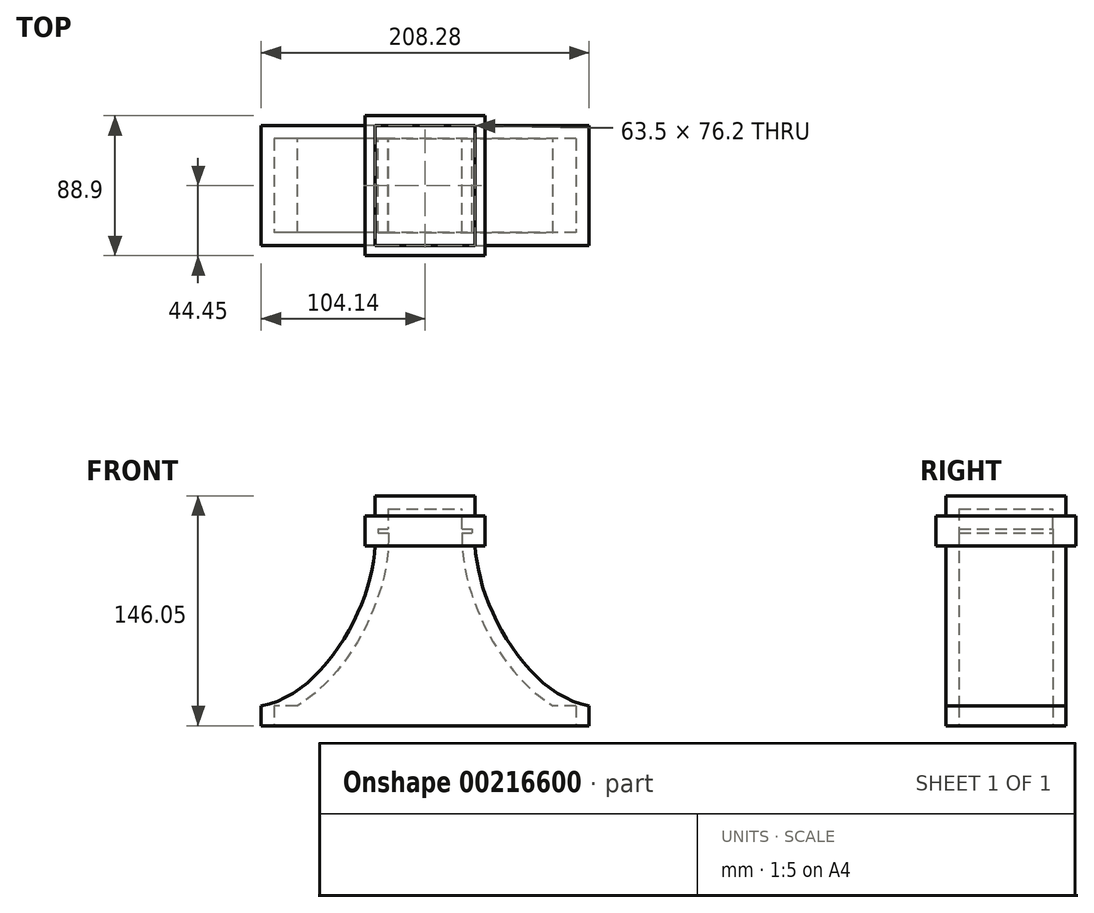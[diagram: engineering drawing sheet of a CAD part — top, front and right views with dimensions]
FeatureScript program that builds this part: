
annotation { "Feature Type Name" : "Feature", "Feature Type Description" : "" }
export const myFeature = defineFeature(function(context is Context, id is Id, definition is map)
    precondition{}
    {
        {
            var Q0;
            Q0=qCreatedBy(makeId("Top.planeOp"),FACE);
            var sketch = newSketch(context, id + "F0", { "sketchPlane" : qUnion([Q0])});
            skLineSegment(sketch, "E0.bottom", {"start": v(104.14, -38.1) * mm, "end": v(-104.14, -38.1) * mm});
            skLineSegment(sketch, "E0.top", {"start": v(104.14, 38.1) * mm, "end": v(-104.14, 38.1) * mm});
            skLineSegment(sketch, "E0.left", {"start": v(104.14, -38.1) * mm, "end": v(104.14, 38.1) * mm});
            skLineSegment(sketch, "E0.right", {"start": v(-104.14, -38.1) * mm, "end": v(-104.14, 38.1) * mm});
            skPoint(sketch, "E0.middle", {"position": v(0, 0) * mm});
            skLineSegment(sketch, "E1.bottom", {"start": v(95.88, 29.85) * mm, "end": v(-95.88, 29.85) * mm});
            skLineSegment(sketch, "E1.top", {"start": v(95.88, -29.85) * mm, "end": v(-95.88, -29.85) * mm});
            skLineSegment(sketch, "E1.left", {"start": v(95.88, 29.84) * mm, "end": v(95.88, -29.85) * mm});
            skLineSegment(sketch, "E1.right", {"start": v(-95.88, 29.85) * mm, "end": v(-95.88, -29.84) * mm});
            skSolve(sketch);
        }
        {
            var Q0;
            Q0=makeQuery(id+"F0.imprint","IMPRINT",FACE,{"disambiguationData":[TD([[makeQuery(id+"F0.imprint","IMPRINT",EDGE,{"derivedFrom":sQuery(id+"F0.wireOp",EDGE,"E0.bottom")}),-1.0]])]});
            extrude(context, id + "F1", {"entities" : qUnion([Q0]), "depth" : 12.7 * mm});
        }
        {
            var Q0;
            Q0=qCreatedBy(makeId("Front.planeOp"),FACE);
            var sketch = newSketch(context, id + "F2", { "sketchPlane" : qUnion([Q0])});
            skLineSegment(sketch, "E2", {"start": v(0, 0) * mm, "end": v(0, 146.05) * mm, "construction": true});
            skLineSegment(sketch, "E3", {"start": v(-31.75, 146.05) * mm, "end": v(31.75, 146.05) * mm});
            skLineSegment(sketch, "E4", {"start": v(-31.75, 146.05) * mm, "end": v(-31.75, 133.35) * mm});
            skLineSegment(sketch, "E5", {"start": v(-31.75, 133.35) * mm, "end": v(31.75, 133.35) * mm});
            skLineSegment(sketch, "E6", {"start": v(31.75, 133.35) * mm, "end": v(31.75, 146.05) * mm});
            skLineSegment(sketch, "E7.bottom", {"start": v(-38.1, 133.35) * mm, "end": v(38.1, 133.35) * mm});
            skLineSegment(sketch, "E7.top", {"start": v(-38.1, 114.3) * mm, "end": v(38.1, 114.3) * mm});
            skLineSegment(sketch, "E7.left", {"start": v(-38.1, 133.35) * mm, "end": v(-38.1, 114.3) * mm});
            skLineSegment(sketch, "E7.right", {"start": v(38.1, 133.35) * mm, "end": v(38.1, 114.3) * mm});
            skPoint(sketch, "E8", {"position": v(0, 114.3) * mm});
            skLineSegment(sketch, "E9", {"start": v(-31.75, 133.35) * mm, "end": v(-31.75, 114.3) * mm, "construction": true});
            skLineSegment(sketch, "E10", {"start": v(31.75, 133.35) * mm, "end": v(31.75, 114.3) * mm, "construction": true});
            skLineSegment(sketch, "E11", {"start": v(-104.14, 12.7) * mm, "end": v(104.14, 12.7) * mm});
            skFitSpline(sketch, "E12", {"points": [v(-31.75, 114.3) * mm, v(-104.14, 12.7) * mm], "startDerivative": vector(-3.4, -108.29) * mm, "endDerivative": vector(-120.63, -20.5) * mm});
            skFitSpline(sketch, "E13.MirrorCS", {"points": [v(31.75, 114.3) * mm, v(104.14, 12.7) * mm], "startDerivative": vector(3.4, -108.29) * mm, "endDerivative": vector(120.63, -20.5) * mm});
            skSolve(sketch);
        }
        {
            var Q0;
            Q0 = qSketchRegion(id + "F2", true);
            var Q1;
            Q1=makeQuery(id+"F1.opExtrude","SWEPT_FACE",FACE,{"disambiguationData":[OSD([sQuery(id+"F0.wireOp",EDGE,"E0.bottom")])]});
            var Q2;
            Q2=makeQuery(id+"F1.opExtrude","SWEPT_FACE",FACE,{"disambiguationData":[OSD([sQuery(id+"F0.wireOp",EDGE,"E0.top")])]});
            extrude(context, id + "F3", {"entities" : qUnion([Q0]), "endBound" : BoundingType.UP_TO_SURFACE, "endBoundEntityFace" : qUnion([Q1]), "depth" : 25.4 * mm, "hasSecondDirection" : true, "secondDirectionBound" : SecondDirectionBoundingType.UP_TO_SURFACE, "secondDirectionOppositeDirection" : true, "secondDirectionBoundEntityFace" : qUnion([Q2]), "secondDirectionDepth" : 25.4 * mm});
        }
        {
            var Q0;
            Q0=makeQuery(id+"F3.opExtrude","SWEPT_FACE",FACE,{"disambiguationData":[OSD([sQuery(id+"F2.wireOp",EDGE,"E11")])]});
            shell(context, id + "F4", {"entities" : qUnion([Q0]), "thickness" : 8.25 * mm});
        }
        {
            var Q0;
            Q0=makeQuery(id+"F1.opExtrude","SWEPT_BODY",BODY,{"disambiguationData":[OSD([sQuery(id+"F0.wireOp",EDGE,"E0.bottom"),sQuery(id+"F0.wireOp",EDGE,"E0.top"),sQuery(id+"F0.wireOp",EDGE,"E0.left"),sQuery(id+"F0.wireOp",EDGE,"E0.right"),sQuery(id+"F0.wireOp",EDGE,"E1.bottom"),sQuery(id+"F0.wireOp",EDGE,"E1.top"),sQuery(id+"F0.wireOp",EDGE,"E1.left"),sQuery(id+"F0.wireOp",EDGE,"E1.right")])]});
            var Q1;
            Q1=makeQuery(id+"F3.opExtrude","SWEPT_BODY",BODY,{"disambiguationData":[OSD([sQuery(id+"F2.wireOp",EDGE,"E3"),sQuery(id+"F2.wireOp",EDGE,"E4"),sQuery(id+"F2.wireOp",EDGE,"E6"),sQuery(id+"F2.wireOp",EDGE,"E7.bottom"),sQuery(id+"F2.wireOp",EDGE,"E7.top"),sQuery(id+"F2.wireOp",EDGE,"E7.left"),sQuery(id+"F2.wireOp",EDGE,"E7.right"),sQuery(id+"F2.wireOp",EDGE,"E11"),sQuery(id+"F2.wireOp",EDGE,"E12"),sQuery(id+"F2.wireOp",EDGE,"E13.MirrorCS")])]});
            booleanBodies(context, id + "F5", {"operationType" : BooleanOperationType.UNION, "tools" : qUnion([Q0, Q1])});
        }
        {
            var Q0;
            {var subQ0=sQuery(id+"F0.wireOp",EDGE,"E0.top");Q0=makeQuery(id+"F5.opBoolean","MERGE",FACE,{"derivedFrom":[makeQuery(id+"F1.opExtrude","SWEPT_FACE",FACE,{"disambiguationData":[OSD([subQ0])]}),makeQuery(id+"F3.opExtrude","CAP_FACE",FACE,{"disambiguationData":[OSD([subQ0])],"isStart":true})]});}
            var sketch = newSketch(context, id + "F6", { "sketchPlane" : qUnion([Q0])});
            skLineSegment(sketch, "E14.bottom", {"start": v(-38.1, 133.35) * mm, "end": v(38.1, 133.35) * mm});
            skLineSegment(sketch, "E14.top", {"start": v(-38.1, 114.3) * mm, "end": v(38.1, 114.3) * mm});
            skLineSegment(sketch, "E14.left", {"start": v(-38.1, 133.35) * mm, "end": v(-38.1, 114.3) * mm});
            skLineSegment(sketch, "E14.right", {"start": v(38.1, 133.35) * mm, "end": v(38.1, 114.3) * mm});
            skSolve(sketch);
        }
        {
            var Q0;
            Q0 = qSketchRegion(id + "F6", true);
            extrude(context, id + "F7", {"entities" : qUnion([Q0]), "operationType" : NewBodyOperationType.ADD, "depth" : 6.35 * mm});
        }
        {
            var Q0;
            {var subQ0=sQuery(id+"F0.wireOp",EDGE,"E0.bottom");Q0=makeQuery(id+"F5.opBoolean","MERGE",FACE,{"derivedFrom":[makeQuery(id+"F1.opExtrude","SWEPT_FACE",FACE,{"disambiguationData":[OSD([subQ0])]}),makeQuery(id+"F3.opExtrude","CAP_FACE",FACE,{"disambiguationData":[OSD([subQ0])],"isStart":false})]});}
            var sketch = newSketch(context, id + "F8", { "sketchPlane" : qUnion([Q0])});
            skLineSegment(sketch, "E15.bottom", {"start": v(-38.1, 133.35) * mm, "end": v(38.1, 133.35) * mm});
            skLineSegment(sketch, "E15.top", {"start": v(-38.1, 114.3) * mm, "end": v(38.1, 114.3) * mm});
            skLineSegment(sketch, "E15.left", {"start": v(-38.1, 133.35) * mm, "end": v(-38.1, 114.3) * mm});
            skLineSegment(sketch, "E15.right", {"start": v(38.1, 133.35) * mm, "end": v(38.1, 114.3) * mm});
            skSolve(sketch);
        }
        {
            var Q0;
            Q0 = qSketchRegion(id + "F8", true);
            extrude(context, id + "F9", {"entities" : qUnion([Q0]), "operationType" : NewBodyOperationType.ADD, "depth" : 6.35 * mm});
        }
    });
